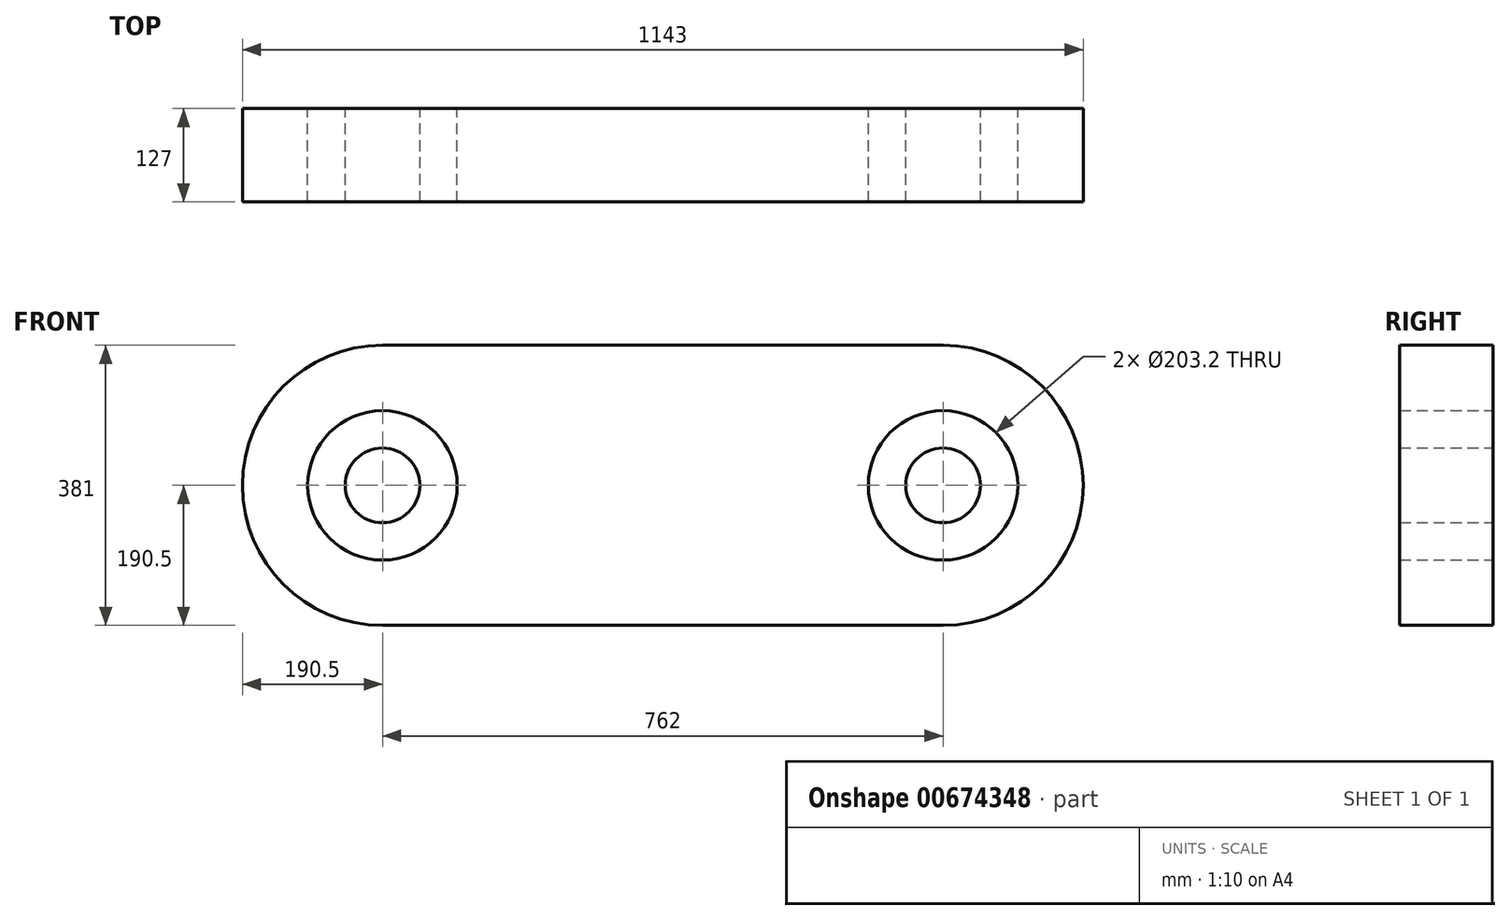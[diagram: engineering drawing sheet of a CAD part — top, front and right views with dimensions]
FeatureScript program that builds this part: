
annotation { "Feature Type Name" : "Feature", "Feature Type Description" : "" }
export const myFeature = defineFeature(function(context is Context, id is Id, definition is map)
    precondition{}
    {
        {
            var Q0;
            Q0=qCreatedBy(makeId("Front.planeOp"),FACE);
            var sketch = newSketch(context, id + "F0", { "sketchPlane" : qUnion([Q0])});
            skLineSegment(sketch, "E0.bottom", {"start": v(0, 0) * mm, "end": v(762, 0) * mm});
            skLineSegment(sketch, "E0.top", {"start": v(0, 381) * mm, "end": v(762, 381) * mm});
            skArc(sketch, "E1", {"start": v(762, 0) * mm, "mid": v(952.5, 190.5) * mm, "end": v(762, 381) * mm});
            skArc(sketch, "E2", {"start": v(0, 381) * mm, "mid": v(-190.5, 190.5) * mm, "end": v(0, 0) * mm});
            skCircle(sketch, "E3", {"center": v(0, 190.5) * mm, "radius": 101.6 * mm});
            skCircle(sketch, "E4", {"center": v(762, 190.5) * mm, "radius": 101.6 * mm});
            skCircle(sketch, "E5", {"center": v(0, 190.5) * mm, "radius": 50.8 * mm});
            skCircle(sketch, "E6", {"center": v(762, 190.5) * mm, "radius": 50.8 * mm});
            skSolve(sketch);
        }
        {
            var Q0;
            Q0=makeQuery(id+"F0.imprint","IMPRINT",FACE,{"disambiguationData":[TD([[makeQuery(id+"F0.imprint","IMPRINT",EDGE,{"derivedFrom":sQuery(id+"F0.wireOp",EDGE,"E0.bottom")}),1.0]])]});
            var Q1;
            Q1=makeQuery(id+"F0.imprint","IMPRINT",FACE,{"disambiguationData":[TD([[makeQuery(id+"F0.imprint","IMPRINT",EDGE,{"derivedFrom":sQuery(id+"F0.wireOp",EDGE,"E5")}),1.0]])]});
            var Q2;
            Q2=makeQuery(id+"F0.imprint","IMPRINT",FACE,{"disambiguationData":[TD([[makeQuery(id+"F0.imprint","IMPRINT",EDGE,{"derivedFrom":sQuery(id+"F0.wireOp",EDGE,"E6")}),1.0]])]});
            extrude(context, id + "F1", {"entities" : qUnion([Q0, Q1, Q2]), "depth" : 127 * mm, "offsetDistance" : 25.4 * mm});
        }
    });
